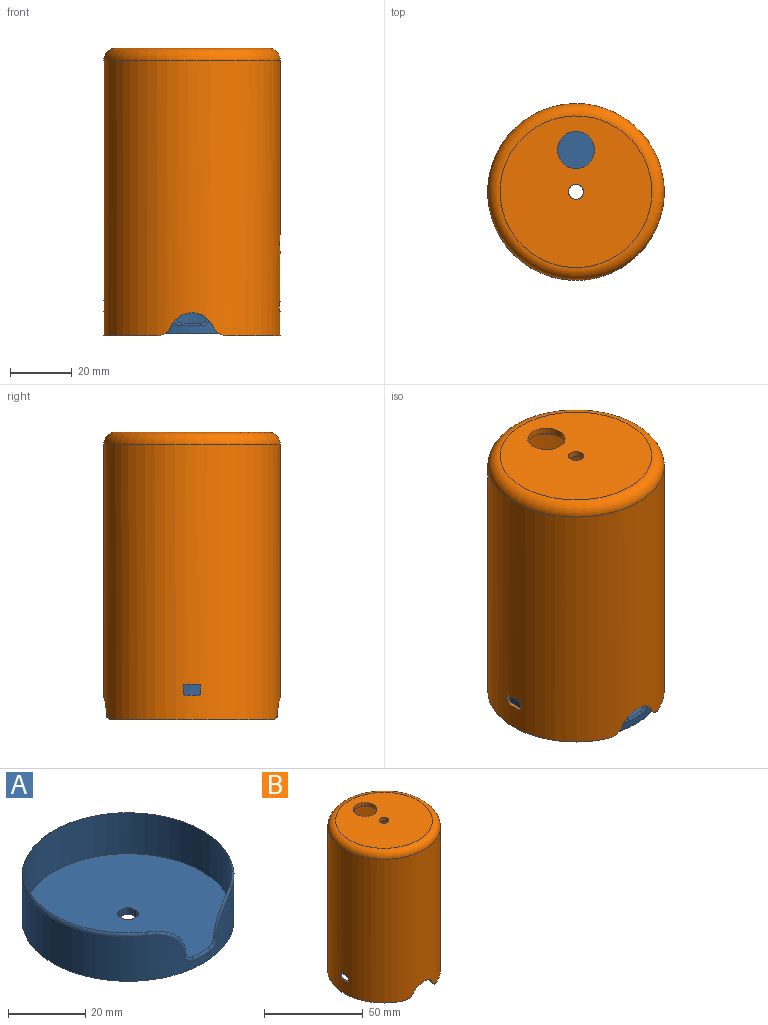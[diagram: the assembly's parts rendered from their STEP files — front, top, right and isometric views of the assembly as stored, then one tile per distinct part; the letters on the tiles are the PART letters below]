
ASSEMBLY  parts=2 mates=1
PART A: 30 faces, bbox 59.5x57.4x15.1 mm
  f0: plane 55x55mm, normal (0,0,-1), area 1974.1mm2, adj f3,f18,f19,f20,f21,f22,f23,f24
  f1: plane 54x54mm, normal (0,0,1), area 2268.7mm2, adj f2,f22,f23,f24,f25,f26,f27,f28
  f2: cylinder r=27mm len=54mm, axis (0,0,-1), area 2047.2mm2, adj f1,f4,f5,f6,f7,f8,f9
  f3: cylinder r=27.5mm len=55mm, axis (0,0,-1), area 2271.9mm2, adj f0,f4,f5,f6,f7,f8,f9
  f4: torus R=26.5mm, axis (0,0,1), area 146.1mm2, adj f2,f3,f5,f6
  f5: bspline ~10.85x10.32mm, area 16.5mm2, adj f2,f3,f4,f7
  f6: bspline ~11.47x10.57mm, area 16.6mm2, adj f2,f3,f4,f8
  f7: bspline ~2.96x2.81mm, area 3.9mm2, adj f2,f3,f5,f9
  f8: bspline ~2.97x2.81mm, area 3.9mm2, adj f2,f3,f6,f9
  f9: torus R=26.5mm, axis (0,0,1), area 6.4mm2, adj f2,f3,f7,f8
  f10: cylinder r=5mm len=10mm, axis (0,0,-1), area 15.7mm2, adj f11,f18
  f11: plane 10x10mm, normal (0,0,-1), area 78.5mm2, adj f10
  f12: cylinder r=5mm len=10mm, axis (0,0,-1), area 15.7mm2, adj f13,f19
  f13: plane 10x10mm, normal (0,0,-1), area 78.5mm2, adj f12
  f14: cylinder r=5mm len=10mm, axis (0,0,-1), area 15.7mm2, adj f15,f20
  f15: plane 10x10mm, normal (0,0,-1), area 78.5mm2, adj f14
  f16: cylinder r=5mm len=10mm, axis (0,0,-1), area 15.7mm2, adj f17,f21
  f17: plane 10x10mm, normal (0,0,-1), area 78.5mm2, adj f16
  f18: torus R=5.5mm, axis (0,0,1), area 25.6mm2, adj f0,f10
  f19: torus R=5.5mm, axis (0,0,1), area 25.6mm2, adj f0,f12
  f20: torus R=5.5mm, axis (0,0,1), area 25.6mm2, adj f0,f14
  f21: torus R=5.5mm, axis (0,0,1), area 25.6mm2, adj f0,f16
  f22: plane 2x1mm, normal (0,-1,0), area 2mm2, adj f0,f1,f26,f29
  f23: plane 2x1mm, normal (-1,0,0), area 2mm2, adj f0,f1,f26,f27
  f24: plane 2x1mm, normal (0,1,0), area 2mm2, adj f0,f1,f27,f28
  f25: plane 2x1mm, normal (1,0,0), area 2mm2, adj f0,f1,f28,f29
  f26: cylinder r=2mm len=2mm, axis (0,0,-1), area 6.3mm2, adj f0,f1,f22,f23
  f27: cylinder r=2mm len=2mm, axis (0,0,1), area 6.3mm2, adj f0,f1,f23,f24
  f28: cylinder r=2mm len=2mm, axis (0,0,-1), area 6.3mm2, adj f0,f1,f24,f25
  f29: cylinder r=2mm len=2mm, axis (0,0,1), area 6.3mm2, adj f0,f1,f22,f25
PART B: 35 faces, bbox 61.7x61.7x93 mm
  f0: plane 52.19x17.04mm, normal (0,0,-1), area 64.4mm2, adj f1,f2,f22,f23
  f1: cylinder r=28.5mm len=89mm, axis (0,0,-1), area 15665.4mm2, adj f0,f7,f8,f9,f10,f11,f12,f13
  f2: cylinder r=27.5mm len=86mm, axis (0,0,-1), area 14587.7mm2, adj f0,f7,f9,f10,f11,f12,f13,f14
  f3: plane 47x47mm, normal (0,0,-1), area 1544.1mm2, adj f6,f19,f34
  f4: plane 49x49mm, normal (0,0,1), area 1754.1mm2, adj f5,f8,f18
  f5: cylinder r=2.43mm len=4.85mm, axis (0,0,1), area 30.5mm2, adj f4,f6
  f6: cone r=3.43mm half-angle=45deg, axis (0,0,-1), area 26mm2, adj f3,f5
  f7: plane 52.19x17.04mm, normal (0,0,-1), area 64.4mm2, adj f1,f2,f24,f25
  f8: torus R=24.5mm, axis (0,0,1), area 1067.8mm2, adj f1,f4
  f9: cylinder r=3.4mm len=6.8mm, axis (1,0,0), area 21.4mm2, adj f1,f2
  f10: plane 6.5x1.19mm, normal (0,0,1), area 6.5mm2, adj f1,f2,f14,f17
  f11: plane 1.25x1.01mm, normal (0,-1,0), area 1.3mm2, adj f1,f2,f14,f15
  f12: plane 6.5x1.19mm, normal (0,0,-1), area 6.5mm2, adj f1,f2,f15,f16
  f13: plane 1.25x1.01mm, normal (0,1,0), area 1.3mm2, adj f1,f2,f16,f17
  f14: cylinder r=1mm len=1.14mm, axis (1,0,0), area 1.6mm2, adj f1,f2,f10,f11
  f15: cylinder r=1mm len=1.14mm, axis (-1,0,0), area 1.6mm2, adj f1,f2,f11,f12
  f16: cylinder r=1mm len=1.14mm, axis (1,0,0), area 1.6mm2, adj f1,f2,f12,f13
  f17: cylinder r=1mm len=1.14mm, axis (-1,0,0), area 1.6mm2, adj f1,f2,f10,f13
  f18: cylinder r=6mm len=12mm, axis (0,0,1), area 75.4mm2, adj f4,f19
  f19: cone r=7mm half-angle=45deg, axis (0,0,-1), area 57.8mm2, adj f3,f18
  f20: cylinder r=7.5mm len=13.75mm, axis (0,-1,0), area 17.6mm2, adj f1,f2,f22,f25
  f21: cylinder r=7.5mm len=13.75mm, axis (0,-1,0), area 17.6mm2, adj f1,f2,f23,f24
  f22: cylinder r=5mm len=4.58mm, axis (0,-1,0), area 6.1mm2, adj f0,f1,f2,f20
  f23: cylinder r=5mm len=4.58mm, axis (0,-1,0), area 6.1mm2, adj f0,f1,f2,f21
  f24: cylinder r=5mm len=4.58mm, axis (0,-1,0), area 6.1mm2, adj f1,f2,f7,f21
  f25: cylinder r=5mm len=4.58mm, axis (0,-1,0), area 6.1mm2, adj f1,f2,f7,f20
  f26: plane 2.5x1.01mm, normal (0,1,0), area 2.5mm2, adj f1,f2,f30,f33
  f27: plane 4.6x1.1mm, normal (0,0,1), area 4.6mm2, adj f1,f2,f30,f31
  f28: plane 2.5x1.01mm, normal (0,-1,0), area 2.5mm2, adj f1,f2,f31,f32
  f29: plane 4.6x1.1mm, normal (0,0,-1), area 4.6mm2, adj f1,f2,f32,f33
  f30: cylinder r=0.5mm len=1.05mm, axis (-1,0,0), area 0.8mm2, adj f1,f2,f26,f27
  f31: cylinder r=0.5mm len=1.05mm, axis (1,0,0), area 0.8mm2, adj f1,f2,f27,f28
  f32: cylinder r=0.5mm len=1.05mm, axis (-1,0,0), area 0.8mm2, adj f1,f2,f28,f29
  f33: cylinder r=0.5mm len=1.05mm, axis (1,0,0), area 0.8mm2, adj f1,f2,f26,f29
  f34: torus R=23.5mm, axis (0,0,1), area 1028.3mm2, adj f2,f3
PLACE A t=(-62.26,80.95,-67.26)mm
PLACE B t=(-62.26,80.95,-68.06)mm
MATE slider B.f1 <-> A.f3  axis (0,0,-1) through (-62.26,80.95,-23.56)mm
